# Revit family: Incepa_Thema_Ducha Higiênica Sem Derivação_B5001I4CRB
name_source: partatom
category: Plumbing Fixtures
revit_build: Autodesk Revit Architecture 2014 (Build: 20131024_2115(x64)
units: mm (PartAtom-declared; Revit-internal decimal feet)

## types (1)
- Sem derivação
    Assembly Code = D2010
    CW Connection = No
    CWFU = 1
    Cost = 0 $
    Default Elevation = 0 mm  [stored 0 ft]
    Description = Ducha higiênica sem derivação com flexível em PVC (B5001I4CRB), linha Thema - Metais Incepa
    Desenvolvido por = ofcdesk
    HW Connection = No
    HWFU = 0
    Incepa: Categoria = Lavatório
    Incepa: Cores Disponíveis = Cromado
    Incepa: Código = B5001I4CRB
    Incepa: Descrição = Ducha higiênica sem derivação com flexível em PVC (B5001I4CRBB), linha Thema - Metais Incepa
    Incepa: Fabricante = Incepa
    Incepa: Linha = Thema
    Incepa: Norma = ABNT NBR 14877:2002 - Requisitos e métodos de ensaio
    Incepa: Produto = Metais
    Incepa: Tipo = Duchas Higiênicas
    Incepa: Versão = Autodesk Revit MEP 2014
    Manufacturer = Incepa
    Model = B5001I4CRB
    Selo de Qualidade ofcdesk = Standard
    URL = http://www.incepa.com.br
    Vent Connection = No
    WFU = 0
    Waste Connection = No

note: [stored X ft] marks values corroborated as IEEE doubles in the binary element streams (Revit-internal decimal feet)

## geometry (parser evidence)
native form markers: Blend x4, Sweep x2
no freeform markers — native parametric forms only
